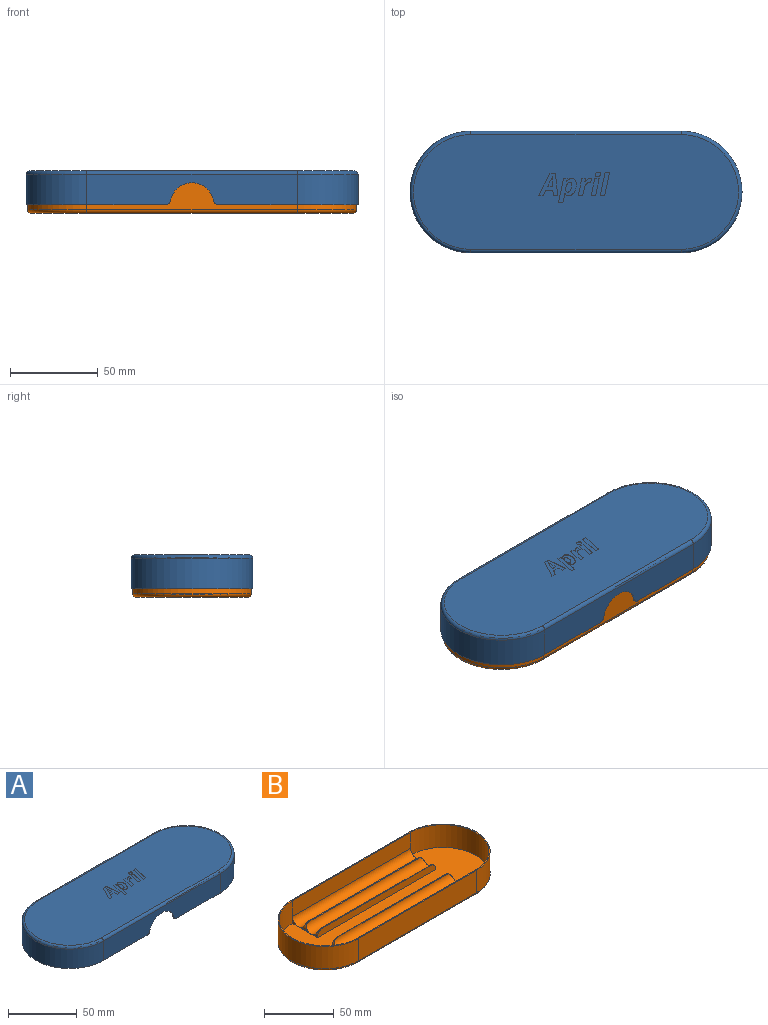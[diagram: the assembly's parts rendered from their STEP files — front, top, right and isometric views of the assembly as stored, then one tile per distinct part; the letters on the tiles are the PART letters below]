
ASSEMBLY  parts=2 mates=1
PART A: 96 faces, bbox 195.1x75.1x19.2 mm
  f0: plane 185.4x65.4mm, normal (0,0,1), area 10956.1mm2, adj f14,f15,f16,f17,f22,f23,f24,f25
  f1: plane 79.49x69.4mm, normal (0,0,-1), area 157.9mm2, adj f2,f4,f5,f7,f8,f9,f18,f19
  f2: plane 120x17.2mm, normal (0,1,0), area 1815.8mm2, adj f1,f3,f5,f10,f13,f15,f19,f20
  f3: cylinder r=34.7mm len=69.4mm, axis (0,0,-1), area 1875mm2, adj f2,f4,f10,f17
  f4: plane 120x17.2mm, normal (0,-1,0), area 1815.8mm2, adj f1,f3,f5,f10,f12,f16,f18,f21
  f5: cylinder r=34.7mm len=69.4mm, axis (0,0,-1), area 1875mm2, adj f1,f2,f4,f14
  f6: cylinder r=33.9mm len=67.8mm, axis (0,0,1), area 1917mm2, adj f7,f9,f10,f11
  f7: plane 120x18mm, normal (0,-1,0), area 1911.8mm2, adj f1,f6,f8,f10,f11,f13,f19,f20
  f8: cylinder r=33.9mm len=67.8mm, axis (0,0,1), area 1917mm2, adj f1,f7,f9,f11
  f9: plane 120x18mm, normal (0,1,0), area 1911.8mm2, adj f1,f6,f8,f10,f11,f12,f18,f21
  f10: plane 79.49x69.4mm, normal (0,0,-1), area 157.9mm2, adj f2,f3,f4,f6,f7,f9,f20,f21
  f11: plane 187.8x67.8mm, normal (0,0,-1), area 11746.3mm2, adj f6,f7,f8,f9
  f12: cylinder r=12.5mm len=24.53mm, axis (0,1,0), area 27.5mm2, adj f4,f9,f18,f21
  f13: cylinder r=12.5mm len=24.53mm, axis (0,1,0), area 27.5mm2, adj f2,f7,f19,f20
  f14: torus R=32.7mm, axis (0,0,1), area 335.3mm2, adj f0,f5,f15,f16
  f15: cylinder r=2mm len=120mm, axis (1,0,0), area 377mm2, adj f0,f2,f14,f17
  f16: cylinder r=2mm len=120mm, axis (-1,0,0), area 377mm2, adj f0,f4,f14,f17
  f17: torus R=32.7mm, axis (0,0,1), area 335.3mm2, adj f0,f3,f15,f16
  f18: cylinder r=3mm len=2.94mm, axis (0,1,0), area 3.3mm2, adj f1,f4,f9,f12
  f19: cylinder r=3mm len=2.94mm, axis (0,1,0), area 3.3mm2, adj f1,f2,f7,f13
  f20: cylinder r=3mm len=2.94mm, axis (0,1,0), area 3.3mm2, adj f2,f7,f10,f13
  f21: cylinder r=3mm len=2.94mm, axis (0,1,0), area 3.3mm2, adj f4,f9,f10,f12
  f22: extruded ~1.29x1.05mm, area 0.4mm2, adj f0,f23,f28,f29
  f23: extruded ~1.16x0.42mm, area 0.3mm2, adj f0,f22,f24,f29
  f24: extruded ~1.1x0.37mm, area 0.2mm2, adj f0,f23,f25,f29
  f25: extruded ~0.76x0.32mm, area 0.2mm2, adj f0,f24,f26,f29
  f26: extruded ~0.95x0.26mm, area 0.2mm2, adj f0,f25,f27,f29
  f27: extruded ~1.15x0.38mm, area 0.2mm2, adj f0,f26,f28,f29
  f28: extruded ~1.12x0.4mm, area 0.2mm2, adj f0,f22,f27,f29
  f29: plane 2.82x2.55mm, normal (0,0,1), area 5.9mm2, adj f22,f23,f24,f25,f26,f27,f28
  f30: plane 9.52x2.02mm, normal (-0.98,0.21,0), area 1.9mm2, adj f0,f31,f33,f34
  f31: plane 2.56x0.2mm, normal (0,-1,0), area 0.5mm2, adj f0,f30,f32,f34
  f32: plane 9.52x2.02mm, normal (0.98,-0.21,0), area 1.9mm2, adj f0,f31,f33,f34
  f33: plane 2.56x0.2mm, normal (0,1,0), area 0.5mm2, adj f0,f30,f32,f34
  f34: plane 9.52x4.58mm, normal (0,0,1), area 24.4mm2, adj f30,f31,f32,f33
  f35: extruded ~3.01x1.94mm, area 0.7mm2, adj f0,f36,f46,f47
  f36: plane 0.2x0.05mm, normal (0,-1,0), area 0mm2, adj f0,f35,f37,f47
  f37: plane 1.76x0.2mm, normal (-0.99,0.1,0), area 0.4mm2, adj f0,f36,f38,f47
  f38: plane 1.96x0.2mm, normal (0,-1,0), area 0.4mm2, adj f0,f37,f39,f47
  f39: plane 9.52x2.02mm, normal (0.98,-0.21,0), area 1.9mm2, adj f0,f38,f40,f47
  f40: plane 2.56x0.2mm, normal (0,1,0), area 0.5mm2, adj f0,f39,f41,f47
  f41: plane 4.26x0.91mm, normal (-0.98,0.21,0), area 0.9mm2, adj f0,f40,f42,f47
  f42: extruded ~2.24x1.06mm, area 0.5mm2, adj f0,f41,f43,f47
  f43: extruded ~1.74x0.78mm, area 0.4mm2, adj f0,f42,f44,f47
  f44: extruded ~0.85x0.2mm, area 0.2mm2, adj f0,f43,f45,f47
  f45: plane 2.47x0.56mm, normal (-0.98,0.22,0), area 0.5mm2, adj f0,f44,f46,f47
  f46: extruded ~0.82x0.2mm, area 0.2mm2, adj f0,f35,f45,f47
  f47: plane 9.7x7.67mm, normal (0,0,1), area 31.4mm2, adj f35,f36,f37,f38,f39,f40,f41,f42
  f48: extruded ~2.7x1.62mm, area 0.7mm2, adj f0,f49,f72,f73
  f49: plane 0.2x0.08mm, normal (0,-1,0), area 0mm2, adj f0,f48,f50,f73
  f50: plane 1.45x0.2mm, normal (-1,0.1,0), area 0.3mm2, adj f0,f49,f51,f73
  f51: plane 1.96x0.2mm, normal (0,-1,0), area 0.4mm2, adj f0,f50,f52,f73
  f52: plane 13.72x2.91mm, normal (0.98,-0.21,0), area 2.8mm2, adj f0,f51,f53,f73
  f53: plane 2.56x0.2mm, normal (0,1,0), area 0.5mm2, adj f0,f52,f54,f73
  f54: plane 2.9x0.61mm, normal (-0.98,0.21,0), area 0.6mm2, adj f0,f53,f55,f73
  f55: extruded ~2.51x0.37mm, area 0.5mm2, adj f0,f54,f56,f73
  f56: plane 0.2x0.07mm, normal (0,1,0), area 0mm2, adj f0,f55,f57,f73
  f57: extruded ~1.07x0.94mm, area 0.3mm2, adj f0,f56,f58,f73
  f58: extruded ~1.22x0.32mm, area 0.3mm2, adj f0,f57,f59,f73
  f59: extruded ~2.23x0.88mm, area 0.5mm2, adj f0,f58,f60,f73
  f60: extruded ~2.39x1.6mm, area 0.6mm2, adj f0,f59,f61,f73
  f61: extruded ~3.13x0.58mm, area 0.6mm2, adj f0,f60,f62,f73
  f62: extruded ~2.56x0.72mm, area 0.5mm2, adj f0,f61,f72,f73
  f63: extruded ~1.5x1.11mm, area 0.4mm2, adj f64,f71,f73,f74
  f64: extruded ~2.02x0.32mm, area 0.4mm2, adj f63,f65,f73,f74
  f65: extruded ~1.61x0.84mm, area 0.4mm2, adj f64,f66,f73,f74
  f66: extruded ~1.09x0.59mm, area 0.3mm2, adj f65,f67,f73,f74
  f67: extruded ~0.87x0.41mm, area 0.2mm2, adj f66,f68,f73,f74
  f68: extruded ~1.09x0.31mm, area 0.2mm2, adj f67,f69,f73,f74
  f69: extruded ~2.12x0.33mm, area 0.4mm2, adj f68,f70,f73,f74
  f70: extruded ~1.53x0.87mm, area 0.4mm2, adj f69,f71,f73,f74
  f71: extruded ~1.12x0.58mm, area 0.3mm2, adj f63,f70,f73,f74
  f72: extruded ~1.96x0.91mm, area 0.4mm2, adj f0,f48,f62,f73
  f73: plane 13.89x10.19mm, normal (0,0,1), area 66.9mm2, adj f48,f49,f50,f51,f52,f53,f54,f55
  f74: plane 5.72x3.43mm, normal (0,0,1), area 14.7mm2, adj f63,f64,f65,f66,f67,f68,f69,f70
  f75: plane 13.25x2.81mm, normal (-0.98,0.21,0), area 2.7mm2, adj f0,f76,f78,f79
  f76: plane 2.56x0.2mm, normal (0,-1,0), area 0.5mm2, adj f0,f75,f77,f79
  f77: plane 13.25x2.81mm, normal (0.98,-0.21,0), area 2.7mm2, adj f0,f76,f78,f79
  f78: plane 2.56x0.2mm, normal (0,1,0), area 0.5mm2, adj f0,f75,f77,f79
  f79: plane 13.25x5.37mm, normal (0,0,1), area 34mm2, adj f75,f76,f77,f78
  f80: plane 2.97x0.2mm, normal (1,0.07,0), area 0.6mm2, adj f0,f81,f93,f94
  f81: plane 2.53x0.2mm, normal (0,1,0), area 0.5mm2, adj f0,f80,f82,f94
  f82: plane 12.5x1.25mm, normal (-1,-0.1,0), area 2.5mm2, adj f0,f81,f83,f94
  f83: plane 3.18x0.2mm, normal (0,-1,0), area 0.6mm2, adj f0,f82,f84,f94
  f84: plane 12.5x6.52mm, normal (0.89,-0.46,0), area 2.8mm2, adj f0,f83,f85,f94
  f85: plane 2.73x0.2mm, normal (0,1,0), area 0.5mm2, adj f0,f84,f86,f94
  f86: plane 2.97x1.46mm, normal (-0.9,0.44,0), area 0.7mm2, adj f0,f85,f93,f94
  f87: plane 2.83x0.2mm, normal (0,-1,0), area 0.6mm2, adj f88,f92,f94,f95
  f88: plane 3.28x1.6mm, normal (-0.9,0.44,0), area 0.7mm2, adj f87,f89,f94,f95
  f89: extruded ~2.16x0.93mm, area 0.5mm2, adj f88,f90,f94,f95
  f90: plane 0.31x0.2mm, normal (1,0,0), area 0.1mm2, adj f89,f91,f94,f95
  f91: extruded ~2.15x0.2mm, area 0.4mm2, adj f90,f92,f94,f95
  f92: plane 2.98x0.22mm, normal (1,0.07,0), area 0.6mm2, adj f87,f91,f94,f95
  f93: plane 4.03x0.2mm, normal (0,1,0), area 0.8mm2, adj f0,f80,f86,f94
  f94: plane 12.5x10.95mm, normal (0,0,1), area 66.6mm2, adj f80,f81,f82,f83,f84,f85,f86,f87
  f95: plane 5.44x2.83mm, normal (0,0,1), area 7.3mm2, adj f87,f88,f89,f90,f91,f92
PART B: 45 faces, bbox 193.2x73.2x21.6 mm
  f0: plane 12.8x1mm, normal (-1,0,0), area 8.3mm2, adj f25,f29,f30,f40
  f1: plane 6x6mm, normal (-1,0,0), area 7.7mm2, adj f20,f25,f30
  f2: plane 6.6x1mm, normal (-1,0,0), area 4.3mm2, adj f25,f29,f31,f41
  f3: plane 12.8x1mm, normal (-1,0,0), area 8.3mm2, adj f25,f27,f28,f43
  f4: plane 6.6x1mm, normal (-1,0,0), area 4.3mm2, adj f25,f28,f32,f42
  f5: plane 6x6mm, normal (-1,0,0), area 7.7mm2, adj f20,f25,f27
  f6: plane 12.8x1mm, normal (1,0,0), area 8.3mm2, adj f25,f29,f30,f37
  f7: plane 6x6mm, normal (1,0,0), area 7.7mm2, adj f22,f25,f30
  f8: plane 6.6x1mm, normal (1,0,0), area 4.3mm2, adj f25,f29,f31,f38
  f9: plane 12.8x1mm, normal (1,0,0), area 8.3mm2, adj f25,f27,f28,f44
  f10: plane 6.6x1mm, normal (1,0,0), area 4.3mm2, adj f25,f28,f32,f39
  f11: plane 6x6mm, normal (1,0,0), area 7.7mm2, adj f22,f25,f27
  f12: plane 110x0.6mm, normal (0,0,1), area 66mm2, adj f29,f31,f38,f41
  f13: plane 110x0.6mm, normal (0,0,1), area 66mm2, adj f28,f32,f39,f42
  f14: plane 110x0.8mm, normal (0,0,1), area 88mm2, adj f27,f28,f43,f44
  f15: plane 120x19.6mm, normal (0,1,0), area 2352mm2, adj f16,f18,f24,f33
  f16: cylinder r=33.8mm len=67.6mm, axis (0,0,1), area 2081.2mm2, adj f15,f17,f24,f34
  f17: plane 120x19.6mm, normal (0,-1,0), area 2352mm2, adj f16,f18,f24,f36
  f18: cylinder r=33.8mm len=67.6mm, axis (0,0,1), area 2081.2mm2, adj f15,f17,f24,f35
  f19: plane 183.6x63.6mm, normal (0,0,-1), area 10808.9mm2, adj f33,f34,f35,f36
  f20: cylinder r=33mm len=66mm, axis (0,0,-1), area 2073.5mm2, adj f1,f5,f21,f23,f24,f25
  f21: plane 120x14mm, normal (0,-1,0), area 1680mm2, adj f20,f22,f24,f27
  f22: cylinder r=33mm len=66mm, axis (0,0,-1), area 2073.5mm2, adj f7,f11,f21,f23,f24,f25
  f23: plane 120x14mm, normal (0,1,0), area 1680mm2, adj f20,f22,f24,f30
  f24: plane 187.6x67.6mm, normal (0,0,1), area 359.9mm2, adj f15,f16,f17,f18,f20,f21,f22,f23
  f25: plane 186x66mm, normal (0,0,1), area 5245.2mm2, adj f0,f1,f2,f3,f4,f5,f6,f7
  f26: plane 110x0.8mm, normal (0,0,1), area 88mm2, adj f29,f30,f37,f40
  f27: cylinder r=6mm len=120mm, axis (-1,0,0), area 2250.8mm2, adj f3,f5,f9,f11,f14,f21,f43,f44
  f28: cylinder r=6mm len=120mm, axis (-1,0,0), area 2239.7mm2, adj f3,f4,f9,f10,f13,f14,f39,f42
  f29: cylinder r=6mm len=120mm, axis (-1,0,0), area 2239.7mm2, adj f0,f2,f6,f8,f12,f26,f37,f38
  f30: cylinder r=6mm len=120mm, axis (-1,0,0), area 2250.8mm2, adj f0,f1,f6,f7,f23,f26,f37,f40
  f31: plane 120x6mm, normal (0,1,0), area 709.3mm2, adj f2,f8,f12,f25,f38,f41
  f32: plane 120x6mm, normal (0,-1,0), area 709.3mm2, adj f4,f10,f13,f25,f39,f42
  f33: cylinder r=2mm len=120mm, axis (1,0,0), area 377mm2, adj f15,f19,f34,f35
  f34: torus R=31.8mm, axis (0,0,1), area 326.4mm2, adj f16,f19,f33,f36
  f35: torus R=31.8mm, axis (0,0,1), area 326.4mm2, adj f18,f19,f33,f36
  f36: cylinder r=2mm len=120mm, axis (-1,0,0), area 377mm2, adj f17,f19,f34,f35
  f37: cylinder r=5mm len=6.17mm, axis (0,-1,0), area 14.7mm2, adj f6,f26,f29,f30
  f38: cylinder r=5mm len=5mm, axis (0,-1,0), area 8.9mm2, adj f8,f12,f29,f31
  f39: cylinder r=5mm len=5mm, axis (0,-1,0), area 8.9mm2, adj f10,f13,f28,f32
  f40: cylinder r=5mm len=6.17mm, axis (0,1,0), area 14.7mm2, adj f0,f26,f29,f30
  f41: cylinder r=5mm len=5mm, axis (0,1,0), area 8.9mm2, adj f2,f12,f29,f31
  f42: cylinder r=5mm len=5mm, axis (0,1,0), area 8.9mm2, adj f4,f13,f28,f32
  f43: cylinder r=5mm len=6.17mm, axis (0,1,0), area 14.7mm2, adj f3,f14,f27,f28
  f44: cylinder r=5mm len=6.17mm, axis (0,-1,0), area 14.7mm2, adj f9,f14,f27,f28
PLACE A at identity
PLACE B t=(5.01,0,38.8)mm
MATE slider B.f16 <-> A.f3  axis (0,0,1) through (-60.5,0,49)mm
